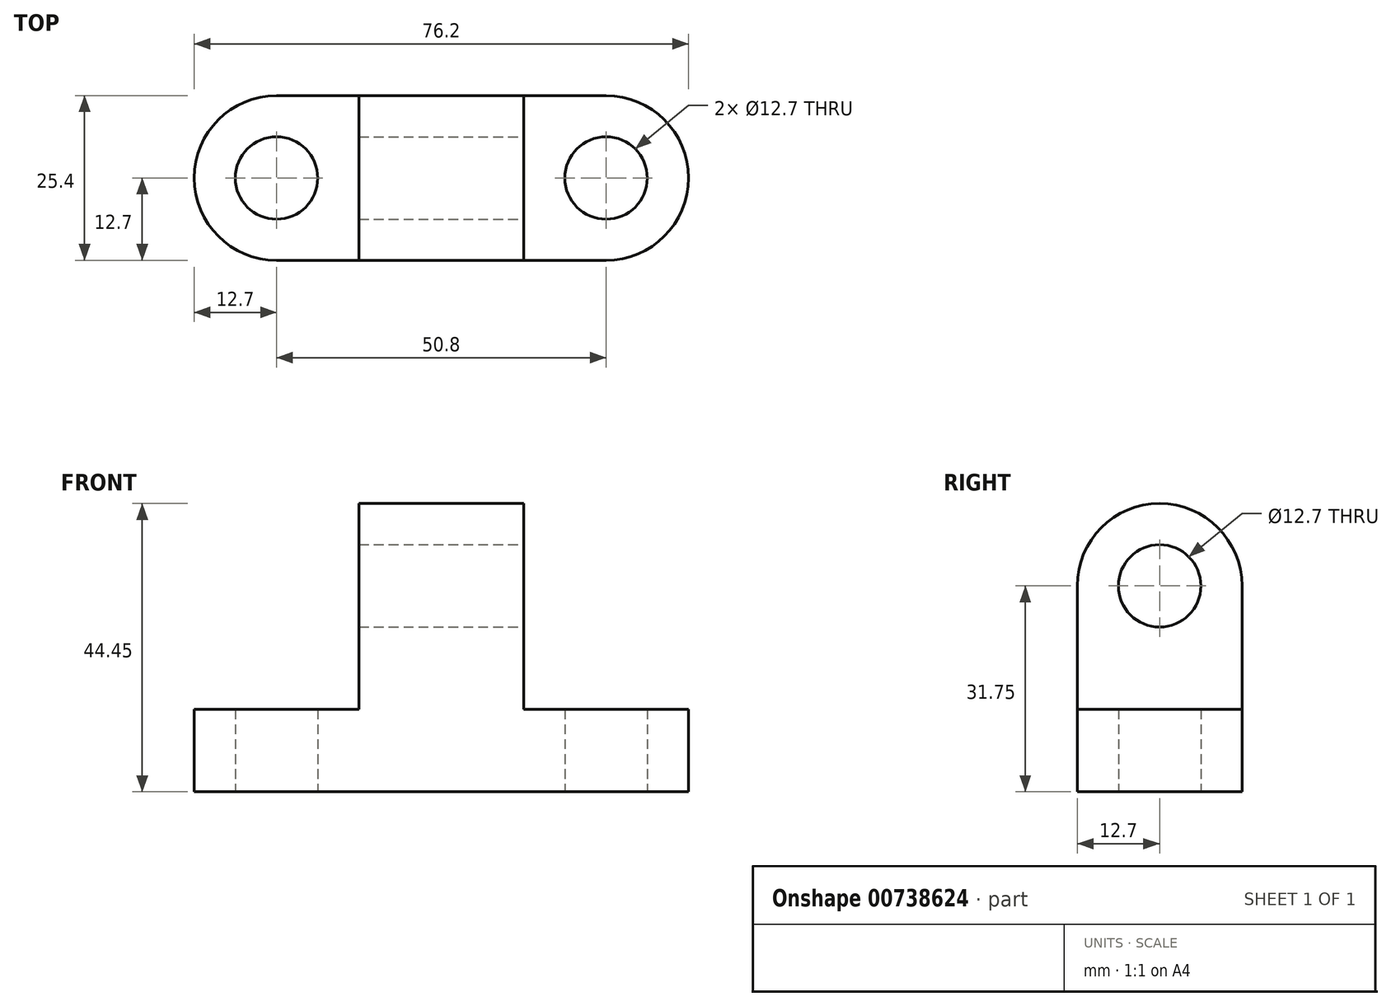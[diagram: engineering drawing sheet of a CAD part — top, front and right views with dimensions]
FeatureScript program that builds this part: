
annotation { "Feature Type Name" : "Feature", "Feature Type Description" : "" }
export const myFeature = defineFeature(function(context is Context, id is Id, definition is map)
    precondition{}
    {
        {
            var Q0;
            Q0=qCreatedBy(makeId("Top.planeOp"),FACE);
            var sketch = newSketch(context, id + "F0", { "sketchPlane" : qUnion([Q0])});
            skLineSegment(sketch, "E0.bottom", {"start": v(0, 0) * mm, "end": v(76.2, 0) * mm});
            skLineSegment(sketch, "E0.top", {"start": v(0, 25.4) * mm, "end": v(76.2, 25.4) * mm});
            skLineSegment(sketch, "E0.left", {"start": v(0, 0) * mm, "end": v(0, 25.4) * mm});
            skLineSegment(sketch, "E0.right", {"start": v(76.2, 0) * mm, "end": v(76.2, 25.4) * mm});
            skLineSegment(sketch, "E1", {"start": v(0, 12.7) * mm, "end": v(12.7, 12.7) * mm});
            skLineSegment(sketch, "E2", {"start": v(76.2, 12.7) * mm, "end": v(63.5, 12.7) * mm});
            skCircle(sketch, "E3", {"center": v(12.7, 12.7) * mm, "radius": 12.7 * mm});
            skCircle(sketch, "E4", {"center": v(63.5, 12.7) * mm, "radius": 12.7 * mm});
            skCircle(sketch, "E5", {"center": v(12.7, 12.7) * mm, "radius": 6.35 * mm});
            skCircle(sketch, "E6", {"center": v(63.5, 12.7) * mm, "radius": 6.35 * mm});
            skSolve(sketch);
        }
        {
            var Q0;
            Q0=makeQuery(id+"F0.imprint","IMPRINT",FACE,{"disambiguationData":[TD([[makeQuery(id+"F0.imprint","IMPRINT",EDGE,{"derivedFrom":sQuery(id+"F0.wireOp",EDGE,"E5")}),-1.0]])]});
            var Q1;
            {var subQ0=sQuery(id+"F0.wireOp",EDGE,"E3");var subQ1=sQuery(id+"F0.wireOp",EDGE,"E0.bottom");var subQ2=makeQuery(id+"F0.imprint","INTERSECT",VERTEX,{"derivedFrom":[subQ1,subQ0]});Q1=makeQuery(id+"F0.imprint","IMPRINT",FACE,{"disambiguationData":[TD([[makeQuery(id+"F0.imprint","IMPRINT",EDGE,{"disambiguationData":[TD([[subQ2,-1.0]])],"derivedFrom":subQ1}),1.0]])]});}
            var Q2;
            Q2=makeQuery(id+"F0.imprint","IMPRINT",FACE,{"disambiguationData":[TD([[makeQuery(id+"F0.imprint","IMPRINT",EDGE,{"derivedFrom":sQuery(id+"F0.wireOp",EDGE,"E6")}),-1.0]])]});
            extrude(context, id + "F1", {"entities" : qUnion([Q0, Q1, Q2]), "depth" : 12.7 * mm, "offsetDistance" : 25.4 * mm});
        }
        {
            var Q0;
            Q0=makeQuery(id+"F1.opExtrude","CAP_FACE",FACE,{"disambiguationData":[OSD([sQuery(id+"F0.wireOp",EDGE,"E0.bottom"),sQuery(id+"F0.wireOp",EDGE,"E0.top"),sQuery(id+"F0.wireOp",EDGE,"E3"),sQuery(id+"F0.wireOp",EDGE,"E4"),sQuery(id+"F0.wireOp",EDGE,"E5"),sQuery(id+"F0.wireOp",EDGE,"E6")])],"isStart":false});
            var sketch = newSketch(context, id + "F2", { "sketchPlane" : qUnion([Q0])});
            skLineSegment(sketch, "E7", {"start": v(63.5, 12.7) * mm, "end": v(50.8, 12.7) * mm});
            skLineSegment(sketch, "E8", {"start": v(12.7, 12.7) * mm, "end": v(25.4, 12.7) * mm});
            skLineSegment(sketch, "E9", {"start": v(50.8, 12.7) * mm, "end": v(50.8, 0) * mm});
            skLineSegment(sketch, "E10", {"start": v(50.8, 12.7) * mm, "end": v(50.8, 25.4) * mm});
            skLineSegment(sketch, "E11", {"start": v(25.4, 12.7) * mm, "end": v(25.4, 25.4) * mm});
            skLineSegment(sketch, "E12", {"start": v(25.4, 12.7) * mm, "end": v(25.4, 0) * mm});
            skSolve(sketch);
        }
        {
            var Q0;
            {var subQ4=sQuery(id+"F2.wireOp",EDGE,"E9");Q0=makeQuery(id+"F2.imprint","IMPRINT",FACE,{"disambiguationData":[TD([[makeQuery(id+"F2.imprint","IMPRINT",EDGE,{"derivedFrom":subQ4}),-1.0]])]});}
            extrude(context, id + "F3", {"entities" : qUnion([Q0]), "operationType" : NewBodyOperationType.ADD, "depth" : 31.75 * mm, "offsetDistance" : 25.4 * mm});
        }
        {
            var Q0;
            Q0=makeQuery(id+"F3.opExtrude","SWEPT_FACE",FACE,{"disambiguationData":[OSD([sQuery(id+"F2.wireOp",EDGE,"E9"),sQuery(id+"F2.wireOp",EDGE,"E10")])]});
            var sketch = newSketch(context, id + "F4", { "sketchPlane" : qUnion([Q0])});
            skLineSegment(sketch, "E13", {"start": v(12.7, 12.7) * mm, "end": v(12.7, 31.75) * mm});
            skCircle(sketch, "E14", {"center": v(12.7, 31.75) * mm, "radius": 6.35 * mm});
            skCircle(sketch, "E15", {"center": v(12.7, 31.75) * mm, "radius": 12.7 * mm});
            skSolve(sketch);
        }
        {
            var Q0;
            {var subQ0=sQuery(id+"F4.wireOp",EDGE,"E15");var subQ1=sQuery(id+"F2.wireOp",EDGE,"E9");var subQ2=makeQuery(id+"F3.opExtrude","CAP_EDGE",EDGE,{"disambiguationData":[OSD([subQ1,sQuery(id+"F2.wireOp",EDGE,"E10")])],"isStart":false});var subQ3=makeQuery(id+"F4.imprint","INTERSECT",VERTEX,{"derivedFrom":[subQ2,subQ0]});Q0=makeQuery(id+"F4.imprint","IMPRINT",FACE,{"disambiguationData":[TD([[makeQuery(id+"F4.imprint","IMPRINT",EDGE,{"disambiguationData":[TD([[subQ3,-1.0]])],"derivedFrom":subQ0}),-1.0]])]});}
            var Q1;
            {var subQ0=sQuery(id+"F4.wireOp",EDGE,"E15");var subQ1=sQuery(id+"F2.wireOp",EDGE,"E10");var subQ2=makeQuery(id+"F3.opExtrude","CAP_EDGE",EDGE,{"disambiguationData":[OSD([sQuery(id+"F2.wireOp",EDGE,"E9"),subQ1])],"isStart":false});var subQ3=makeQuery(id+"F4.imprint","INTERSECT",VERTEX,{"derivedFrom":[subQ2,subQ0]});Q1=makeQuery(id+"F4.imprint","IMPRINT",FACE,{"disambiguationData":[TD([[makeQuery(id+"F4.imprint","IMPRINT",EDGE,{"disambiguationData":[TD([[subQ3,1.0]])],"derivedFrom":subQ0}),-1.0]])]});}
            var Q2;
            Q2=makeQuery(id+"F4.imprint","IMPRINT",FACE,{"disambiguationData":[TD([[makeQuery(id+"F4.imprint","IMPRINT",EDGE,{"derivedFrom":sQuery(id+"F4.wireOp",EDGE,"E14")}),1.0]])]});
            extrude(context, id + "F5", {"entities" : qUnion([Q0, Q1, Q2]), "operationType" : NewBodyOperationType.REMOVE, "endBound" : BoundingType.THROUGH_ALL, "oppositeDirection" : true, "depth" : 25.4 * mm, "offsetDistance" : 25.4 * mm});
        }
    });
